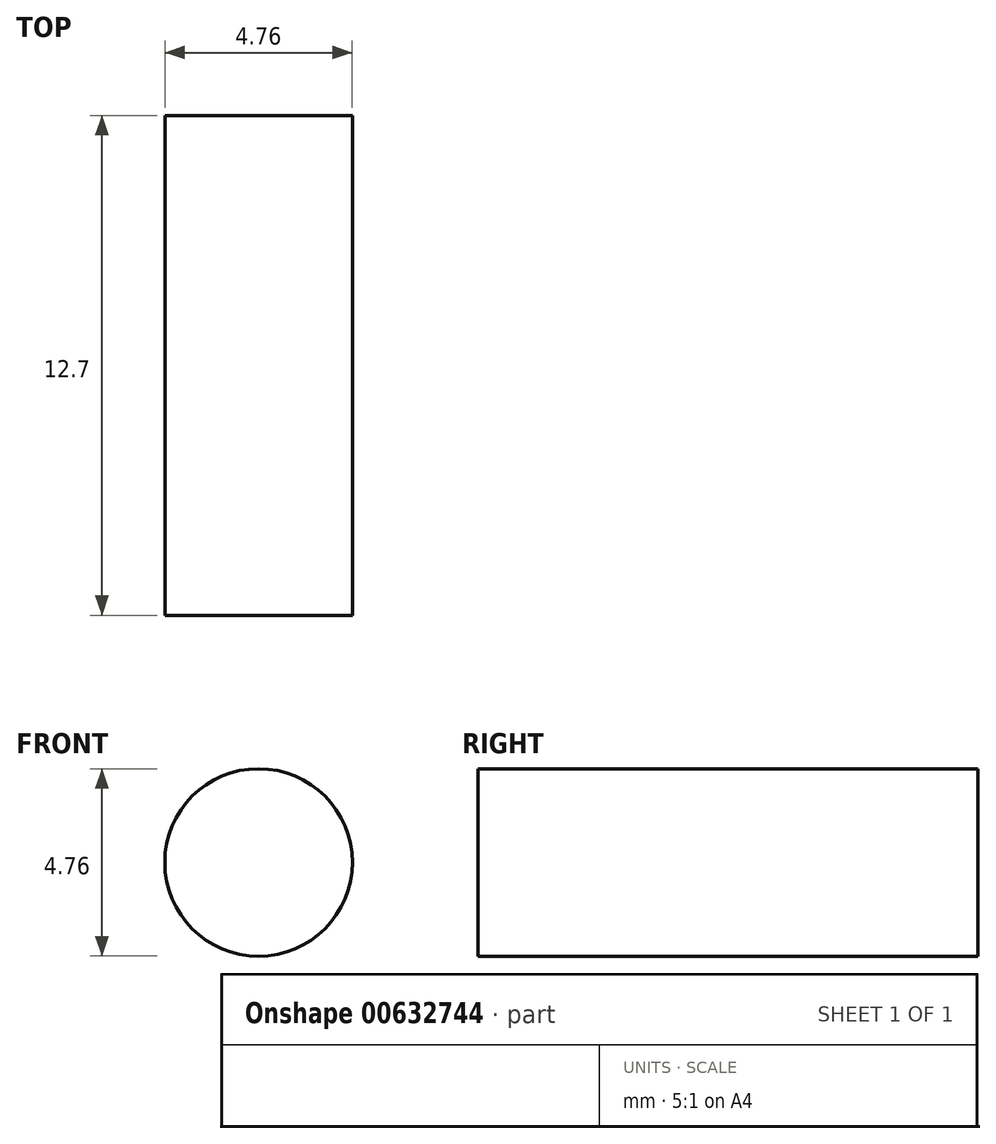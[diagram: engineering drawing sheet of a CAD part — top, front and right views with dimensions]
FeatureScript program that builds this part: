
annotation { "Feature Type Name" : "Feature", "Feature Type Description" : "" }
export const myFeature = defineFeature(function(context is Context, id is Id, definition is map)
    precondition{}
    {
        {
            var Q0;
            Q0=qCreatedBy(makeId("Front.planeOp"),FACE);
            var sketch = newSketch(context, id + "F0", { "sketchPlane" : qUnion([Q0])});
            skCircle(sketch, "E0", {"center": v(0, 0) * mm, "radius": 2.38 * mm});
            skSolve(sketch);
        }
        {
            var Q0;
            Q0 = qSketchRegion(id + "F0", true);
            extrude(context, id + "F1", {"entities" : qUnion([Q0]), "depth" : 12.7 * mm, "offsetDistance" : 25.4 * mm});
        }
        {
            var Q0;
            Q0=qCreatedBy(makeId("Right.planeOp"),FACE);
            var sketch = newSketch(context, id + "F2", { "sketchPlane" : qUnion([Q0])});
            skLineSegment(sketch, "E1", {"start": v(-12.7, 2.38) * mm, "end": v(0, 2.38) * mm});
            skSolve(sketch);
        }
    });
